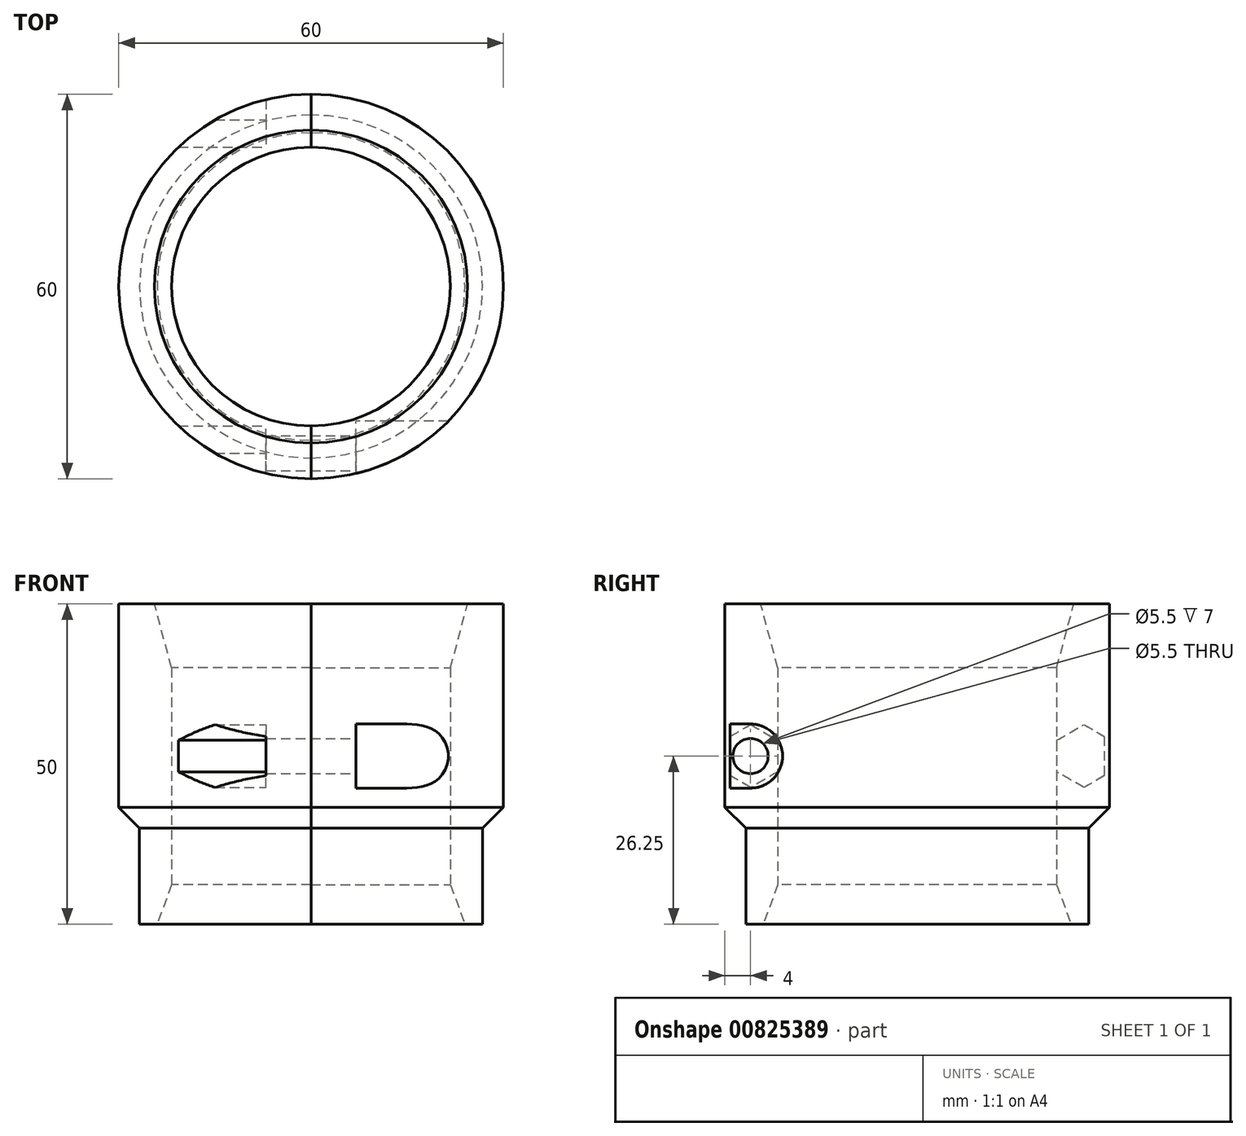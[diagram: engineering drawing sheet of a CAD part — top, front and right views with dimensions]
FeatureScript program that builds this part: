
annotation { "Feature Type Name" : "Feature", "Feature Type Description" : "" }
export const myFeature = defineFeature(function(context is Context, id is Id, definition is map)
    precondition{}
    {
        {
            var Q0;
            Q0=qCreatedBy(makeId("Right.planeOp"),FACE);
            var sketch = newSketch(context, id + "F0", { "sketchPlane" : qUnion([Q0])});
            skLineSegment(sketch, "E0", {"start": v(-26.75, 15) * mm, "end": v(-26.75, 0) * mm});
            skLineSegment(sketch, "E1", {"start": v(-21.75, 40) * mm, "end": v(-21.75, 6.18) * mm});
            skLineSegment(sketch, "E2", {"start": v(-21.75, 6.18) * mm, "end": v(-24, 0) * mm});
            skLineSegment(sketch, "E3", {"start": v(-24, 0) * mm, "end": v(-26.75, 0) * mm});
            skLineSegment(sketch, "E4", {"start": v(0, 0) * mm, "end": v(0, 54.23) * mm});
            skLineSegment(sketch, "E5", {"start": v(-26.75, 15) * mm, "end": v(-30, 18.25) * mm});
            skLineSegment(sketch, "E6", {"start": v(-30, 18.25) * mm, "end": v(-30, 50) * mm});
            skLineSegment(sketch, "E7", {"start": v(-21.75, 40) * mm, "end": v(-24.43, 50) * mm});
            skLineSegment(sketch, "E8", {"start": v(-24.43, 50) * mm, "end": v(-30, 50) * mm});
            skSolve(sketch);
        }
        {
            var Q0;
            Q0=makeQuery(id+"F0.imprint","IMPRINT",FACE,{"disambiguationData":[TD([[makeQuery(id+"F0.imprint","IMPRINT",EDGE,{"derivedFrom":sQuery(id+"F0.wireOp",EDGE,"E0")}),1.0]])]});
            var Q1;
            Q1=sQuery(id+"F0.wireOp",EDGE,"E4");
            revolve(context, id + "F1", {"surfaceOperationType" : NewSurfaceOperationType.NEW, "entities" : qUnion([Q0]), "axis" : qUnion([Q1]), "revolveType" : RevolveType.ONE_DIRECTION, "angle" : 180 * degree});
        }
        {
            var Q0;
            Q0=qCreatedBy(makeId("Right.planeOp"),FACE);
            cPlane(context, id + "F2", {"entities" : qUnion([Q0]), "cplaneType" : CPlaneType.OFFSET, "offset" : 7 * mm, "width" : 150 * mm, "height" : 150 * mm});
        }
        {
            var Q0;
            Q0=makeQuery(id+"F1.opRevolve","SWEPT_BODY",BODY,{"disambiguationData":[OSD([sQuery(id+"F0.wireOp",EDGE,"E0"),sQuery(id+"F0.wireOp",EDGE,"E1"),sQuery(id+"F0.wireOp",EDGE,"E2"),sQuery(id+"F0.wireOp",EDGE,"E3"),sQuery(id+"F0.wireOp",EDGE,"E5"),sQuery(id+"F0.wireOp",EDGE,"E6"),sQuery(id+"F0.wireOp",EDGE,"E7"),sQuery(id+"F0.wireOp",EDGE,"E8")])]});
            var Q1;
            Q1=qCreatedBy(makeId("Right.planeOp"),FACE);
            mirror(context, id + "F3", {"entities" : qUnion([Q0]), "mirrorPlane" : qUnion([Q1])});
        }
        {
            var Q0;
            Q0=qCreatedBy(id+"F2.planeOp",FACE);
            var sketch = newSketch(context, id + "F4", { "sketchPlane" : qUnion([Q0])});
            skLineSegment(sketch, "E9", {"start": v(-26, 31.25) * mm, "end": v(-30, 31.25) * mm});
            skLineSegment(sketch, "E10", {"start": v(-30, 31.25) * mm, "end": v(-30, 21.25) * mm});
            skLineSegment(sketch, "E11", {"start": v(-30, 21.25) * mm, "end": v(-26, 21.25) * mm});
            skArc(sketch, "E12", {"start": v(-26, 21.25) * mm, "mid": v(-21, 26.25) * mm, "end": v(-26, 31.25) * mm});
            skCircle(sketch, "E13", {"center": v(-26, 26.25) * mm, "radius": 2.75 * mm, "construction": true});
            skSolve(sketch);
        }
        {
            var Q0;
            Q0 = qSketchRegion(id + "F4", true);
            extrude(context, id + "F5", {"entities" : qUnion([Q0]), "operationType" : NewBodyOperationType.REMOVE, "depth" : 82.4 * mm, "offsetDistance" : 25 * mm});
        }
        {
            var Q0;
            Q0=makeQuery(id+"F5.boolean.opBoolean","COPY",FACE,{"derivedFrom":makeQuery(id+"F5.opExtrude","CAP_FACE",FACE,{"disambiguationData":[OSD([sQuery(id+"F4.wireOp",EDGE,"E9"),sQuery(id+"F4.wireOp",EDGE,"E10"),sQuery(id+"F4.wireOp",EDGE,"E11"),sQuery(id+"F4.wireOp",EDGE,"E12")])],"isStart":true})});
            var sketch = newSketch(context, id + "F6", { "sketchPlane" : qUnion([Q0])});
            skPoint(sketch, "E14", {"position": v(-26, 26.25) * mm});
            skSolve(sketch);
        }
        {
            var Q0;
            Q0=sQuery(id+"F6.wireOp",VERTEX,"E14");
            var Q1;
            Q1=makeQuery(id+"F3.opPattern","COPY",BODY,{"derivedFrom":makeQuery(id+"F1.opRevolve","SWEPT_BODY",BODY,{"disambiguationData":[OSD([sQuery(id+"F0.wireOp",EDGE,"E0"),sQuery(id+"F0.wireOp",EDGE,"E1"),sQuery(id+"F0.wireOp",EDGE,"E2"),sQuery(id+"F0.wireOp",EDGE,"E3"),sQuery(id+"F0.wireOp",EDGE,"E5"),sQuery(id+"F0.wireOp",EDGE,"E6"),sQuery(id+"F0.wireOp",EDGE,"E7"),sQuery(id+"F0.wireOp",EDGE,"E8")])]}),"instanceName":"1"});
            var Q2;
            Q2=makeQuery(id+"F1.opRevolve","SWEPT_BODY",BODY,{"disambiguationData":[OSD([sQuery(id+"F0.wireOp",EDGE,"E0"),sQuery(id+"F0.wireOp",EDGE,"E1"),sQuery(id+"F0.wireOp",EDGE,"E2"),sQuery(id+"F0.wireOp",EDGE,"E3"),sQuery(id+"F0.wireOp",EDGE,"E5"),sQuery(id+"F0.wireOp",EDGE,"E6"),sQuery(id+"F0.wireOp",EDGE,"E7"),sQuery(id+"F0.wireOp",EDGE,"E8")])]});
            hole(context, id + "F7", {"style" : HoleStyle.SIMPLE, "endStyle" : HoleEndStyle.THROUGH, "holeDiameter" : 5.5 * mm, "majorDiameter" : 5 * mm, "isTappedThrough" : true, "tappedDepth" : 12 * mm, "tapClearance" : 3, "locations" : qUnion([Q0]), "scope" : qUnion([Q1, Q2])});
        }
        {
            var Q0;
            Q0=qCreatedBy(makeId("Right.planeOp"),FACE);
            cPlane(context, id + "F8", {"entities" : qUnion([Q0]), "cplaneType" : CPlaneType.OFFSET, "offset" : 7 * mm, "oppositeDirection" : true, "width" : 150 * mm, "height" : 150 * mm});
        }
        {
            var Q0;
            Q0=qCreatedBy(id+"F8.planeOp",FACE);
            var sketch = newSketch(context, id + "F9", { "sketchPlane" : qUnion([Q0])});
            skCircle(sketch, "E15.0", {"center": v(26, 26.25) * mm, "radius": 2.75 * mm, "construction": true});
            skCircle(sketch, "E16.0", {"center": v(-26, 26.25) * mm, "radius": 2.75 * mm, "construction": true});
            skCircle(sketch, "E17.cCircle", {"center": v(-26, 26.25) * mm, "radius": 4.25 * mm, "construction": true});
            skLineSegment(sketch, "E17.0", {"start": v(-26, 31.16) * mm, "end": v(-21.75, 28.7) * mm});
            skLineSegment(sketch, "E17.1", {"start": v(-21.75, 28.7) * mm, "end": v(-21.75, 23.8) * mm});
            skLineSegment(sketch, "E17.2", {"start": v(-21.75, 23.8) * mm, "end": v(-26, 21.34) * mm});
            skLineSegment(sketch, "E17.3", {"start": v(-26, 21.34) * mm, "end": v(-30.25, 23.8) * mm});
            skLineSegment(sketch, "E17.4", {"start": v(-30.25, 23.8) * mm, "end": v(-30.25, 28.7) * mm});
            skLineSegment(sketch, "E17.5", {"start": v(-30.25, 28.7) * mm, "end": v(-26, 31.16) * mm});
            skPoint(sketch, "E17.0.midPoint", {"position": v(-23.87, 29.93) * mm});
            skCircle(sketch, "E18.cCircle", {"center": v(26, 26.25) * mm, "radius": 4.25 * mm, "construction": true});
            skLineSegment(sketch, "E18.0", {"start": v(21.75, 23.8) * mm, "end": v(21.75, 28.7) * mm});
            skLineSegment(sketch, "E18.1", {"start": v(21.75, 28.7) * mm, "end": v(26, 31.16) * mm});
            skLineSegment(sketch, "E18.2", {"start": v(26, 31.16) * mm, "end": v(30.25, 28.7) * mm});
            skLineSegment(sketch, "E18.3", {"start": v(30.25, 28.7) * mm, "end": v(30.25, 23.8) * mm});
            skLineSegment(sketch, "E18.4", {"start": v(30.25, 23.8) * mm, "end": v(26, 21.34) * mm});
            skLineSegment(sketch, "E18.5", {"start": v(26, 21.34) * mm, "end": v(21.75, 23.8) * mm});
            skPoint(sketch, "E18.0.midPoint", {"position": v(21.75, 26.25) * mm});
            skSolve(sketch);
        }
        {
            var Q0;
            Q0 = qSketchRegion(id + "F9", true);
            var Q1;
            Q1=sQuery(id+"F9.wireOp",EDGE,"E15.0");
            var Q2;
            Q2=sQuery(id+"F9.wireOp",EDGE,"E16.0");
            extrude(context, id + "F10", {"entities" : qUnion([Q0]), "operationType" : NewBodyOperationType.REMOVE, "surfaceEntities" : qUnion([Q1, Q2]), "oppositeDirection" : true, "depth" : 30 * mm, "offsetDistance" : 25 * mm});
        }
    });
